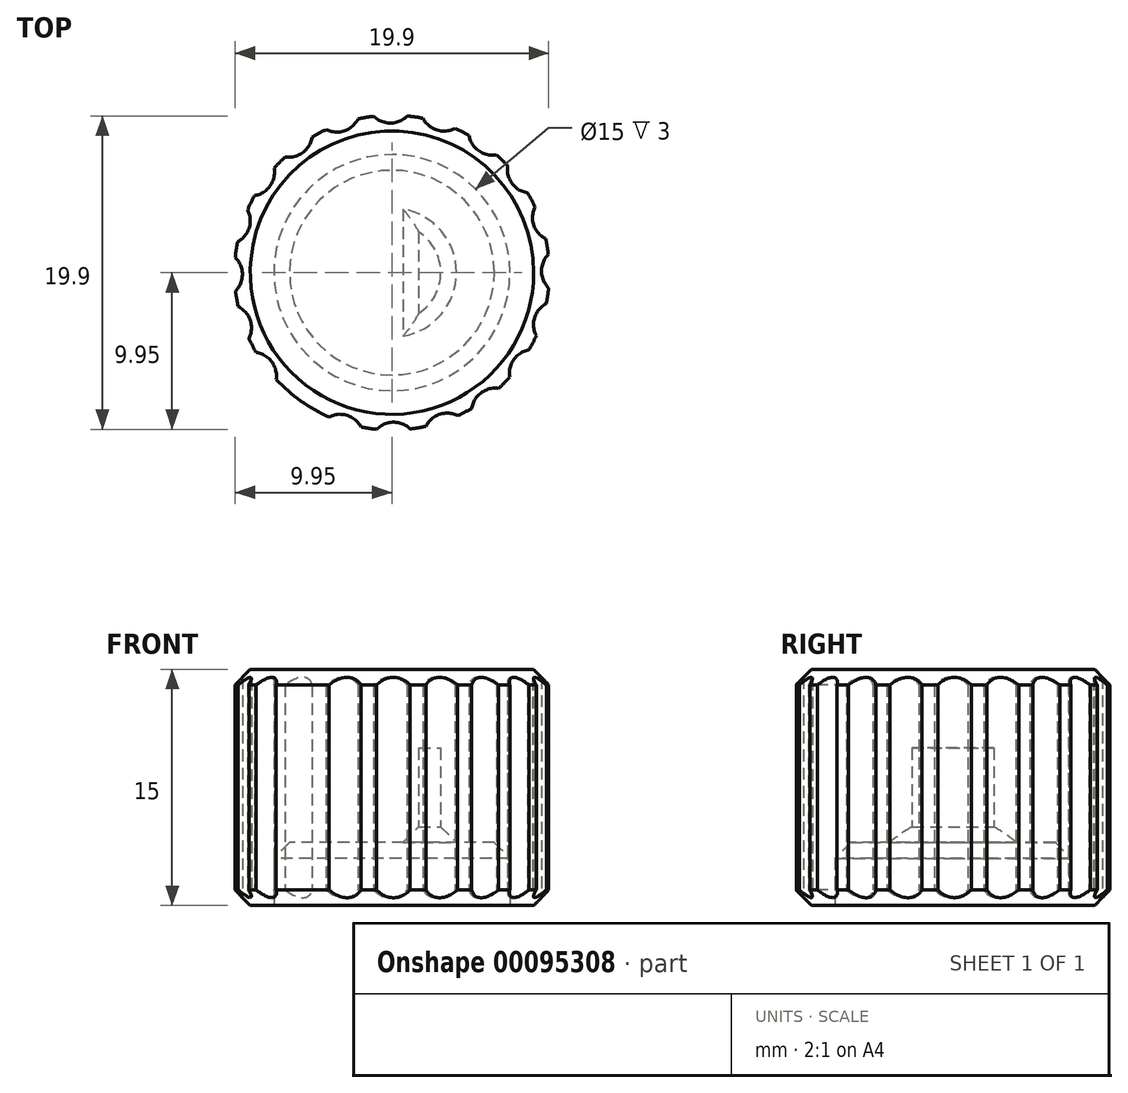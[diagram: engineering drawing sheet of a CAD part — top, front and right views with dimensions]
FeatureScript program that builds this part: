
annotation { "Feature Type Name" : "Feature", "Feature Type Description" : "" }
export const myFeature = defineFeature(function(context is Context, id is Id, definition is map)
    precondition{}
    {
        {
            var Q0;
            Q0=qCreatedBy(makeId("Top.planeOp"),FACE);
            var sketch = newSketch(context, id + "F0", { "sketchPlane" : qUnion([Q0])});
            skCircle(sketch, "E0", {"center": v(0, 0) * mm, "radius": 10 * mm});
            skCircle(sketch, "E1", {"center": v(0, 0) * mm, "radius": 3.1 * mm});
            skLineSegment(sketch, "E2", {"start": v(1.7, 3.51) * mm, "end": v(1.7, -4.44) * mm});
            skCircle(sketch, "E3", {"center": v(0, 0) * mm, "radius": 7.5 * mm});
            skCircle(sketch, "E4", {"center": v(0, 0) * mm, "radius": 11 * mm, "construction": true});
            skCircle(sketch, "E5", {"center": v(10.5, -3.3) * mm, "radius": 1.5 * mm});
            skCircle(sketch, "E6.1.0", {"center": v(11, 0.1) * mm, "radius": 1.5 * mm});
            skCircle(sketch, "E6.2.0", {"center": v(10.43, 3.5) * mm, "radius": 1.5 * mm});
            skCircle(sketch, "E6.3.0", {"center": v(8.83, 6.55) * mm, "radius": 1.5 * mm});
            skCircle(sketch, "E6.4.0", {"center": v(6.38, 8.96) * mm, "radius": 1.5 * mm});
            skCircle(sketch, "E6.5.0", {"center": v(3.3, 10.5) * mm, "radius": 1.5 * mm});
            skCircle(sketch, "E6.6.0", {"center": v(-0.1, 11) * mm, "radius": 1.5 * mm});
            skCircle(sketch, "E6.7.0", {"center": v(-3.5, 10.43) * mm, "radius": 1.5 * mm});
            skCircle(sketch, "E6.8.0", {"center": v(-6.55, 8.83) * mm, "radius": 1.5 * mm});
            skCircle(sketch, "E6.9.0", {"center": v(-8.96, 6.38) * mm, "radius": 1.5 * mm});
            skCircle(sketch, "E6.10.0", {"center": v(-10.5, 3.3) * mm, "radius": 1.5 * mm});
            skCircle(sketch, "E6.11.0", {"center": v(-11, -0.1) * mm, "radius": 1.5 * mm});
            skCircle(sketch, "E6.12.0", {"center": v(-10.43, -3.5) * mm, "radius": 1.5 * mm});
            skCircle(sketch, "E6.13.0", {"center": v(-8.83, -6.55) * mm, "radius": 1.5 * mm});
            skCircle(sketch, "E6.14.0", {"center": v(-6.38, -8.96) * mm, "radius": 1.5 * mm});
            skCircle(sketch, "E6.15.0", {"center": v(-3.3, -10.5) * mm, "radius": 1.5 * mm});
            skCircle(sketch, "E6.16.0", {"center": v(0.1, -11) * mm, "radius": 1.5 * mm});
            skCircle(sketch, "E6.17.0", {"center": v(3.5, -10.43) * mm, "radius": 1.5 * mm});
            skLineSegment(sketch, "E6.anchor1", {"start": v(0, 0) * mm, "end": v(10.5, -3.3) * mm, "construction": true});
            skLineSegment(sketch, "E6.anchor2", {"start": v(0, 0) * mm, "end": v(8.96, -6.38) * mm, "construction": true});
            skCircle(sketch, "E7.1.18.0", {"center": v(6.55, -8.83) * mm, "radius": 1.5 * mm});
            skCircle(sketch, "E7.1.19.0", {"center": v(8.96, -6.38) * mm, "radius": 1.5 * mm});
            skSolve(sketch);
        }
        {
            var Q0;
            {var subQ0=sQuery(id+"F0.wireOp",EDGE,"E2");var subQ1=sQuery(id+"F0.wireOp",EDGE,"E1");var subQ2=makeQuery(id+"F0.imprint","INTERSECT",VERTEX,{"disambiguationData":[OD(0.0)],"derivedFrom":[subQ1,subQ0]});Q0=makeQuery(id+"F0.imprint","IMPRINT",FACE,{"disambiguationData":[TD([[makeQuery(id+"F0.imprint","IMPRINT",EDGE,{"disambiguationData":[TD([[subQ2,-1.0]])],"derivedFrom":subQ1}),1.0]])]});}
            var Q1;
            {var subQ0=sQuery(id+"F0.wireOp",EDGE,"E2");var subQ1=sQuery(id+"F0.wireOp",EDGE,"E1");var subQ2=makeQuery(id+"F0.imprint","INTERSECT",VERTEX,{"disambiguationData":[OD(0.0)],"derivedFrom":[subQ1,subQ0]});Q1=makeQuery(id+"F0.imprint","IMPRINT",FACE,{"disambiguationData":[TD([[makeQuery(id+"F0.imprint","IMPRINT",EDGE,{"disambiguationData":[TD([[subQ2,1.0]])],"derivedFrom":subQ1}),1.0]])]});}
            var Q2;
            Q2=makeQuery(id+"F0.imprint","IMPRINT",FACE,{"disambiguationData":[TD([[makeQuery(id+"F0.imprint","IMPRINT",EDGE,{"derivedFrom":sQuery(id+"F0.wireOp",EDGE,"E3")}),1.0]])]});
            var Q3;
            Q3=makeQuery(id+"F0.imprint","IMPRINT",FACE,{"disambiguationData":[TD([[makeQuery(id+"F0.imprint","IMPRINT",EDGE,{"derivedFrom":sQuery(id+"F0.wireOp",EDGE,"E3")}),-1.0]])]});
            var Q4;
            {var subQ0=sQuery(id+"F0.wireOp",EDGE,"E6.14.0");var subQ1=sQuery(id+"F0.wireOp",EDGE,"E0");var subQ2=makeQuery(id+"F0.imprint","INTERSECT",VERTEX,{"disambiguationData":[OD(0.0)],"derivedFrom":[subQ1,subQ0]});Q4=makeQuery(id+"F0.imprint","IMPRINT",FACE,{"disambiguationData":[TD([[makeQuery(id+"F0.imprint","IMPRINT",EDGE,{"disambiguationData":[TD([[subQ2,-1.0]])],"derivedFrom":subQ1}),1.0]])]});}
            var Q5;
            {var subQ0=sQuery(id+"F0.wireOp",EDGE,"E6.15.0");var subQ1=sQuery(id+"F0.wireOp",EDGE,"E0");var subQ2=makeQuery(id+"F0.imprint","INTERSECT",VERTEX,{"disambiguationData":[OD(0.0)],"derivedFrom":[subQ1,subQ0]});Q5=makeQuery(id+"F0.imprint","IMPRINT",FACE,{"disambiguationData":[TD([[makeQuery(id+"F0.imprint","IMPRINT",EDGE,{"disambiguationData":[TD([[subQ2,-1.0]])],"derivedFrom":subQ1}),1.0]])]});}
            var Q6;
            {var subQ0=sQuery(id+"F0.wireOp",EDGE,"E6.16.0");var subQ1=sQuery(id+"F0.wireOp",EDGE,"E0");var subQ2=makeQuery(id+"F0.imprint","INTERSECT",VERTEX,{"disambiguationData":[OD(0.0)],"derivedFrom":[subQ1,subQ0]});Q6=makeQuery(id+"F0.imprint","IMPRINT",FACE,{"disambiguationData":[TD([[makeQuery(id+"F0.imprint","IMPRINT",EDGE,{"disambiguationData":[TD([[subQ2,-1.0]])],"derivedFrom":subQ1}),1.0]])]});}
            var Q7;
            {var subQ0=sQuery(id+"F0.wireOp",EDGE,"E6.1.0");var subQ1=sQuery(id+"F0.wireOp",EDGE,"E0");var subQ2=makeQuery(id+"F0.imprint","INTERSECT",VERTEX,{"disambiguationData":[OD(0.0)],"derivedFrom":[subQ1,subQ0]});Q7=makeQuery(id+"F0.imprint","IMPRINT",FACE,{"disambiguationData":[TD([[makeQuery(id+"F0.imprint","IMPRINT",EDGE,{"disambiguationData":[TD([[subQ2,1.0]])],"derivedFrom":subQ1}),1.0]])]});}
            var Q8;
            {var subQ0=sQuery(id+"F0.wireOp",EDGE,"E6.2.0");var subQ1=sQuery(id+"F0.wireOp",EDGE,"E0");var subQ2=makeQuery(id+"F0.imprint","INTERSECT",VERTEX,{"disambiguationData":[OD(0.0)],"derivedFrom":[subQ1,subQ0]});Q8=makeQuery(id+"F0.imprint","IMPRINT",FACE,{"disambiguationData":[TD([[makeQuery(id+"F0.imprint","IMPRINT",EDGE,{"disambiguationData":[TD([[subQ2,-1.0]])],"derivedFrom":subQ1}),1.0]])]});}
            var Q9;
            {var subQ0=sQuery(id+"F0.wireOp",EDGE,"E6.17.0");var subQ1=sQuery(id+"F0.wireOp",EDGE,"E0");var subQ2=makeQuery(id+"F0.imprint","INTERSECT",VERTEX,{"disambiguationData":[OD(0.0)],"derivedFrom":[subQ1,subQ0]});Q9=makeQuery(id+"F0.imprint","IMPRINT",FACE,{"disambiguationData":[TD([[makeQuery(id+"F0.imprint","IMPRINT",EDGE,{"disambiguationData":[TD([[subQ2,-1.0]])],"derivedFrom":subQ1}),1.0]])]});}
            var Q10;
            {var subQ0=sQuery(id+"F0.wireOp",EDGE,"E7.1.18.0");var subQ1=sQuery(id+"F0.wireOp",EDGE,"E0");var subQ2=makeQuery(id+"F0.imprint","INTERSECT",VERTEX,{"disambiguationData":[OD(0.0)],"derivedFrom":[subQ1,subQ0]});Q10=makeQuery(id+"F0.imprint","IMPRINT",FACE,{"disambiguationData":[TD([[makeQuery(id+"F0.imprint","IMPRINT",EDGE,{"disambiguationData":[TD([[subQ2,-1.0]])],"derivedFrom":subQ1}),1.0]])]});}
            var Q11;
            {var subQ0=sQuery(id+"F0.wireOp",EDGE,"E6.13.0");var subQ1=sQuery(id+"F0.wireOp",EDGE,"E0");var subQ2=makeQuery(id+"F0.imprint","INTERSECT",VERTEX,{"disambiguationData":[OD(0.0)],"derivedFrom":[subQ1,subQ0]});Q11=makeQuery(id+"F0.imprint","IMPRINT",FACE,{"disambiguationData":[TD([[makeQuery(id+"F0.imprint","IMPRINT",EDGE,{"disambiguationData":[TD([[subQ2,-1.0]])],"derivedFrom":subQ1}),1.0]])]});}
            var Q12;
            {var subQ0=sQuery(id+"F0.wireOp",EDGE,"E6.12.0");var subQ1=sQuery(id+"F0.wireOp",EDGE,"E0");var subQ2=makeQuery(id+"F0.imprint","INTERSECT",VERTEX,{"disambiguationData":[OD(0.0)],"derivedFrom":[subQ1,subQ0]});Q12=makeQuery(id+"F0.imprint","IMPRINT",FACE,{"disambiguationData":[TD([[makeQuery(id+"F0.imprint","IMPRINT",EDGE,{"disambiguationData":[TD([[subQ2,-1.0]])],"derivedFrom":subQ1}),1.0]])]});}
            var Q13;
            {var subQ0=sQuery(id+"F0.wireOp",EDGE,"E6.11.0");var subQ1=sQuery(id+"F0.wireOp",EDGE,"E0");var subQ2=makeQuery(id+"F0.imprint","INTERSECT",VERTEX,{"disambiguationData":[OD(0.0)],"derivedFrom":[subQ1,subQ0]});Q13=makeQuery(id+"F0.imprint","IMPRINT",FACE,{"disambiguationData":[TD([[makeQuery(id+"F0.imprint","IMPRINT",EDGE,{"disambiguationData":[TD([[subQ2,-1.0]])],"derivedFrom":subQ1}),1.0]])]});}
            var Q14;
            {var subQ0=sQuery(id+"F0.wireOp",EDGE,"E6.10.0");var subQ1=sQuery(id+"F0.wireOp",EDGE,"E0");var subQ2=makeQuery(id+"F0.imprint","INTERSECT",VERTEX,{"disambiguationData":[OD(0.0)],"derivedFrom":[subQ1,subQ0]});Q14=makeQuery(id+"F0.imprint","IMPRINT",FACE,{"disambiguationData":[TD([[makeQuery(id+"F0.imprint","IMPRINT",EDGE,{"disambiguationData":[TD([[subQ2,-1.0]])],"derivedFrom":subQ1}),1.0]])]});}
            var Q15;
            {var subQ0=sQuery(id+"F0.wireOp",EDGE,"E6.9.0");var subQ1=sQuery(id+"F0.wireOp",EDGE,"E0");var subQ2=makeQuery(id+"F0.imprint","INTERSECT",VERTEX,{"disambiguationData":[OD(0.0)],"derivedFrom":[subQ1,subQ0]});Q15=makeQuery(id+"F0.imprint","IMPRINT",FACE,{"disambiguationData":[TD([[makeQuery(id+"F0.imprint","IMPRINT",EDGE,{"disambiguationData":[TD([[subQ2,-1.0]])],"derivedFrom":subQ1}),1.0]])]});}
            var Q16;
            {var subQ0=sQuery(id+"F0.wireOp",EDGE,"E6.8.0");var subQ1=sQuery(id+"F0.wireOp",EDGE,"E0");var subQ2=makeQuery(id+"F0.imprint","INTERSECT",VERTEX,{"disambiguationData":[OD(0.0)],"derivedFrom":[subQ1,subQ0]});Q16=makeQuery(id+"F0.imprint","IMPRINT",FACE,{"disambiguationData":[TD([[makeQuery(id+"F0.imprint","IMPRINT",EDGE,{"disambiguationData":[TD([[subQ2,-1.0]])],"derivedFrom":subQ1}),1.0]])]});}
            var Q17;
            {var subQ0=sQuery(id+"F0.wireOp",EDGE,"E6.7.0");var subQ1=sQuery(id+"F0.wireOp",EDGE,"E0");var subQ2=makeQuery(id+"F0.imprint","INTERSECT",VERTEX,{"disambiguationData":[OD(0.0)],"derivedFrom":[subQ1,subQ0]});Q17=makeQuery(id+"F0.imprint","IMPRINT",FACE,{"disambiguationData":[TD([[makeQuery(id+"F0.imprint","IMPRINT",EDGE,{"disambiguationData":[TD([[subQ2,-1.0]])],"derivedFrom":subQ1}),1.0]])]});}
            var Q18;
            {var subQ0=sQuery(id+"F0.wireOp",EDGE,"E6.6.0");var subQ1=sQuery(id+"F0.wireOp",EDGE,"E0");var subQ2=makeQuery(id+"F0.imprint","INTERSECT",VERTEX,{"disambiguationData":[OD(0.0)],"derivedFrom":[subQ1,subQ0]});Q18=makeQuery(id+"F0.imprint","IMPRINT",FACE,{"disambiguationData":[TD([[makeQuery(id+"F0.imprint","IMPRINT",EDGE,{"disambiguationData":[TD([[subQ2,-1.0]])],"derivedFrom":subQ1}),1.0]])]});}
            var Q19;
            {var subQ0=sQuery(id+"F0.wireOp",EDGE,"E6.5.0");var subQ1=sQuery(id+"F0.wireOp",EDGE,"E0");var subQ2=makeQuery(id+"F0.imprint","INTERSECT",VERTEX,{"disambiguationData":[OD(0.0)],"derivedFrom":[subQ1,subQ0]});Q19=makeQuery(id+"F0.imprint","IMPRINT",FACE,{"disambiguationData":[TD([[makeQuery(id+"F0.imprint","IMPRINT",EDGE,{"disambiguationData":[TD([[subQ2,-1.0]])],"derivedFrom":subQ1}),1.0]])]});}
            var Q20;
            {var subQ0=sQuery(id+"F0.wireOp",EDGE,"E6.4.0");var subQ1=sQuery(id+"F0.wireOp",EDGE,"E0");var subQ2=makeQuery(id+"F0.imprint","INTERSECT",VERTEX,{"disambiguationData":[OD(0.0)],"derivedFrom":[subQ1,subQ0]});Q20=makeQuery(id+"F0.imprint","IMPRINT",FACE,{"disambiguationData":[TD([[makeQuery(id+"F0.imprint","IMPRINT",EDGE,{"disambiguationData":[TD([[subQ2,-1.0]])],"derivedFrom":subQ1}),1.0]])]});}
            var Q21;
            {var subQ0=sQuery(id+"F0.wireOp",EDGE,"E7.1.19.0");var subQ1=sQuery(id+"F0.wireOp",EDGE,"E0");var subQ2=makeQuery(id+"F0.imprint","INTERSECT",VERTEX,{"disambiguationData":[OD(0.0)],"derivedFrom":[subQ1,subQ0]});Q21=makeQuery(id+"F0.imprint","IMPRINT",FACE,{"disambiguationData":[TD([[makeQuery(id+"F0.imprint","IMPRINT",EDGE,{"disambiguationData":[TD([[subQ2,-1.0]])],"derivedFrom":subQ1}),1.0]])]});}
            var Q22;
            {var subQ0=sQuery(id+"F0.wireOp",EDGE,"E5");var subQ1=sQuery(id+"F0.wireOp",EDGE,"E0");var subQ2=makeQuery(id+"F0.imprint","INTERSECT",VERTEX,{"disambiguationData":[OD(0.0)],"derivedFrom":[subQ1,subQ0]});Q22=makeQuery(id+"F0.imprint","IMPRINT",FACE,{"disambiguationData":[TD([[makeQuery(id+"F0.imprint","IMPRINT",EDGE,{"disambiguationData":[TD([[subQ2,-1.0]])],"derivedFrom":subQ1}),1.0]])]});}
            var Q23;
            {var subQ0=sQuery(id+"F0.wireOp",EDGE,"E6.3.0");var subQ1=sQuery(id+"F0.wireOp",EDGE,"E0");var subQ2=makeQuery(id+"F0.imprint","INTERSECT",VERTEX,{"disambiguationData":[OD(0.0)],"derivedFrom":[subQ1,subQ0]});Q23=makeQuery(id+"F0.imprint","IMPRINT",FACE,{"disambiguationData":[TD([[makeQuery(id+"F0.imprint","IMPRINT",EDGE,{"disambiguationData":[TD([[subQ2,-1.0]])],"derivedFrom":subQ1}),1.0]])]});}
            extrude(context, id + "F1", {"entities" : qUnion([Q0, Q1, Q2, Q3, Q4, Q5, Q6, Q7, Q8, Q9, Q10, Q11, Q12, Q13, Q14, Q15, Q16, Q17, Q18, Q19, Q20, Q21, Q22, Q23]), "depth" : 15 * mm});
        }
        {
            var Q0;
            {var subQ0=sQuery(id+"F0.wireOp",EDGE,"E2");var subQ1=sQuery(id+"F0.wireOp",EDGE,"E1");var subQ2=makeQuery(id+"F0.imprint","INTERSECT",VERTEX,{"disambiguationData":[OD(0.0)],"derivedFrom":[subQ1,subQ0]});Q0=makeQuery(id+"F0.imprint","IMPRINT",FACE,{"disambiguationData":[TD([[makeQuery(id+"F0.imprint","IMPRINT",EDGE,{"disambiguationData":[TD([[subQ2,1.0]])],"derivedFrom":subQ1}),1.0]])]});}
            extrude(context, id + "F2", {"entities" : qUnion([Q0]), "operationType" : NewBodyOperationType.REMOVE, "depth" : 10 * mm});
        }
        {
            var Q0;
            Q0=makeQuery(id+"F0.imprint","IMPRINT",FACE,{"disambiguationData":[TD([[makeQuery(id+"F0.imprint","IMPRINT",EDGE,{"derivedFrom":sQuery(id+"F0.wireOp",EDGE,"E3")}),1.0]])]});
            var Q1;
            {var subQ0=sQuery(id+"F0.wireOp",EDGE,"E2");var subQ1=sQuery(id+"F0.wireOp",EDGE,"E1");var subQ2=makeQuery(id+"F0.imprint","INTERSECT",VERTEX,{"disambiguationData":[OD(0.0)],"derivedFrom":[subQ1,subQ0]});Q1=makeQuery(id+"F0.imprint","IMPRINT",FACE,{"disambiguationData":[TD([[makeQuery(id+"F0.imprint","IMPRINT",EDGE,{"disambiguationData":[TD([[subQ2,-1.0]])],"derivedFrom":subQ1}),1.0]])]});}
            extrude(context, id + "F3", {"entities" : qUnion([Q0, Q1]), "operationType" : NewBodyOperationType.REMOVE, "depth" : 4 * mm});
        }
        {
            var Q0;
            Q0=makeQuery(id+"F3.boolean.opBoolean","COPY",FACE,{"derivedFrom":makeQuery(id+"F3.opExtrude","CAP_FACE",FACE,{"disambiguationData":[OSD([sQuery(id+"F0.wireOp",EDGE,"E1"),sQuery(id+"F0.wireOp",EDGE,"E2"),sQuery(id+"F0.wireOp",EDGE,"E3")])],"isStart":false})});
            var Q1;
            Q1=makeQuery(id+"F1.opExtrude","CAP_EDGE",EDGE,{"disambiguationData":[OSD([sQuery(id+"F0.wireOp",EDGE,"E0")])],"isStart":false});
            var Q2;
            Q2=makeQuery(id+"F1.opExtrude","CAP_EDGE",EDGE,{"disambiguationData":[OSD([sQuery(id+"F0.wireOp",EDGE,"E0")])],"isStart":true});
            chamfer(context, id + "F4", {"entities" : qUnion([Q0, Q1, Q2]), "width" : 1 * mm, "tangentPropagation" : true});
        }
        {
            var Q0;
            {var subQ0=sQuery(id+"F0.wireOp",EDGE,"E6.16.0");var subQ1=sQuery(id+"F0.wireOp",EDGE,"E0");var subQ2=makeQuery(id+"F0.imprint","INTERSECT",VERTEX,{"disambiguationData":[OD(0.0)],"derivedFrom":[subQ1,subQ0]});Q0=makeQuery(id+"F0.imprint","IMPRINT",FACE,{"disambiguationData":[TD([[makeQuery(id+"F0.imprint","IMPRINT",EDGE,{"disambiguationData":[TD([[subQ2,-1.0]])],"derivedFrom":subQ1}),1.0]])]});}
            var Q1;
            {var subQ0=sQuery(id+"F0.wireOp",EDGE,"E6.17.0");var subQ1=sQuery(id+"F0.wireOp",EDGE,"E0");var subQ2=makeQuery(id+"F0.imprint","INTERSECT",VERTEX,{"disambiguationData":[OD(0.0)],"derivedFrom":[subQ1,subQ0]});Q1=makeQuery(id+"F0.imprint","IMPRINT",FACE,{"disambiguationData":[TD([[makeQuery(id+"F0.imprint","IMPRINT",EDGE,{"disambiguationData":[TD([[subQ2,-1.0]])],"derivedFrom":subQ1}),1.0]])]});}
            var Q2;
            {var subQ0=sQuery(id+"F0.wireOp",EDGE,"E7.1.18.0");var subQ1=sQuery(id+"F0.wireOp",EDGE,"E0");var subQ2=makeQuery(id+"F0.imprint","INTERSECT",VERTEX,{"disambiguationData":[OD(0.0)],"derivedFrom":[subQ1,subQ0]});Q2=makeQuery(id+"F0.imprint","IMPRINT",FACE,{"disambiguationData":[TD([[makeQuery(id+"F0.imprint","IMPRINT",EDGE,{"disambiguationData":[TD([[subQ2,-1.0]])],"derivedFrom":subQ1}),1.0]])]});}
            var Q3;
            {var subQ0=sQuery(id+"F0.wireOp",EDGE,"E7.1.19.0");var subQ1=sQuery(id+"F0.wireOp",EDGE,"E0");var subQ2=makeQuery(id+"F0.imprint","INTERSECT",VERTEX,{"disambiguationData":[OD(0.0)],"derivedFrom":[subQ1,subQ0]});Q3=makeQuery(id+"F0.imprint","IMPRINT",FACE,{"disambiguationData":[TD([[makeQuery(id+"F0.imprint","IMPRINT",EDGE,{"disambiguationData":[TD([[subQ2,-1.0]])],"derivedFrom":subQ1}),1.0]])]});}
            var Q4;
            {var subQ0=sQuery(id+"F0.wireOp",EDGE,"E5");var subQ1=sQuery(id+"F0.wireOp",EDGE,"E0");var subQ2=makeQuery(id+"F0.imprint","INTERSECT",VERTEX,{"disambiguationData":[OD(0.0)],"derivedFrom":[subQ1,subQ0]});Q4=makeQuery(id+"F0.imprint","IMPRINT",FACE,{"disambiguationData":[TD([[makeQuery(id+"F0.imprint","IMPRINT",EDGE,{"disambiguationData":[TD([[subQ2,-1.0]])],"derivedFrom":subQ1}),1.0]])]});}
            var Q5;
            {var subQ0=sQuery(id+"F0.wireOp",EDGE,"E6.1.0");var subQ1=sQuery(id+"F0.wireOp",EDGE,"E0");var subQ2=makeQuery(id+"F0.imprint","INTERSECT",VERTEX,{"disambiguationData":[OD(0.0)],"derivedFrom":[subQ1,subQ0]});Q5=makeQuery(id+"F0.imprint","IMPRINT",FACE,{"disambiguationData":[TD([[makeQuery(id+"F0.imprint","IMPRINT",EDGE,{"disambiguationData":[TD([[subQ2,1.0]])],"derivedFrom":subQ1}),1.0]])]});}
            var Q6;
            {var subQ0=sQuery(id+"F0.wireOp",EDGE,"E6.2.0");var subQ1=sQuery(id+"F0.wireOp",EDGE,"E0");var subQ2=makeQuery(id+"F0.imprint","INTERSECT",VERTEX,{"disambiguationData":[OD(0.0)],"derivedFrom":[subQ1,subQ0]});Q6=makeQuery(id+"F0.imprint","IMPRINT",FACE,{"disambiguationData":[TD([[makeQuery(id+"F0.imprint","IMPRINT",EDGE,{"disambiguationData":[TD([[subQ2,-1.0]])],"derivedFrom":subQ1}),1.0]])]});}
            var Q7;
            {var subQ0=sQuery(id+"F0.wireOp",EDGE,"E6.15.0");var subQ1=sQuery(id+"F0.wireOp",EDGE,"E0");var subQ2=makeQuery(id+"F0.imprint","INTERSECT",VERTEX,{"disambiguationData":[OD(0.0)],"derivedFrom":[subQ1,subQ0]});Q7=makeQuery(id+"F0.imprint","IMPRINT",FACE,{"disambiguationData":[TD([[makeQuery(id+"F0.imprint","IMPRINT",EDGE,{"disambiguationData":[TD([[subQ2,-1.0]])],"derivedFrom":subQ1}),1.0]])]});}
            var Q8;
            {var subQ0=sQuery(id+"F0.wireOp",EDGE,"E6.13.0");var subQ1=sQuery(id+"F0.wireOp",EDGE,"E0");var subQ2=makeQuery(id+"F0.imprint","INTERSECT",VERTEX,{"disambiguationData":[OD(0.0)],"derivedFrom":[subQ1,subQ0]});Q8=makeQuery(id+"F0.imprint","IMPRINT",FACE,{"disambiguationData":[TD([[makeQuery(id+"F0.imprint","IMPRINT",EDGE,{"disambiguationData":[TD([[subQ2,-1.0]])],"derivedFrom":subQ1}),1.0]])]});}
            var Q9;
            {var subQ0=sQuery(id+"F0.wireOp",EDGE,"E6.12.0");var subQ1=sQuery(id+"F0.wireOp",EDGE,"E0");var subQ2=makeQuery(id+"F0.imprint","INTERSECT",VERTEX,{"disambiguationData":[OD(0.0)],"derivedFrom":[subQ1,subQ0]});Q9=makeQuery(id+"F0.imprint","IMPRINT",FACE,{"disambiguationData":[TD([[makeQuery(id+"F0.imprint","IMPRINT",EDGE,{"disambiguationData":[TD([[subQ2,-1.0]])],"derivedFrom":subQ1}),1.0]])]});}
            var Q10;
            {var subQ0=sQuery(id+"F0.wireOp",EDGE,"E6.11.0");var subQ1=sQuery(id+"F0.wireOp",EDGE,"E0");var subQ2=makeQuery(id+"F0.imprint","INTERSECT",VERTEX,{"disambiguationData":[OD(0.0)],"derivedFrom":[subQ1,subQ0]});Q10=makeQuery(id+"F0.imprint","IMPRINT",FACE,{"disambiguationData":[TD([[makeQuery(id+"F0.imprint","IMPRINT",EDGE,{"disambiguationData":[TD([[subQ2,-1.0]])],"derivedFrom":subQ1}),1.0]])]});}
            var Q11;
            {var subQ0=sQuery(id+"F0.wireOp",EDGE,"E6.10.0");var subQ1=sQuery(id+"F0.wireOp",EDGE,"E0");var subQ2=makeQuery(id+"F0.imprint","INTERSECT",VERTEX,{"disambiguationData":[OD(0.0)],"derivedFrom":[subQ1,subQ0]});Q11=makeQuery(id+"F0.imprint","IMPRINT",FACE,{"disambiguationData":[TD([[makeQuery(id+"F0.imprint","IMPRINT",EDGE,{"disambiguationData":[TD([[subQ2,-1.0]])],"derivedFrom":subQ1}),1.0]])]});}
            var Q12;
            {var subQ0=sQuery(id+"F0.wireOp",EDGE,"E6.9.0");var subQ1=sQuery(id+"F0.wireOp",EDGE,"E0");var subQ2=makeQuery(id+"F0.imprint","INTERSECT",VERTEX,{"disambiguationData":[OD(0.0)],"derivedFrom":[subQ1,subQ0]});Q12=makeQuery(id+"F0.imprint","IMPRINT",FACE,{"disambiguationData":[TD([[makeQuery(id+"F0.imprint","IMPRINT",EDGE,{"disambiguationData":[TD([[subQ2,-1.0]])],"derivedFrom":subQ1}),1.0]])]});}
            var Q13;
            {var subQ0=sQuery(id+"F0.wireOp",EDGE,"E6.8.0");var subQ1=sQuery(id+"F0.wireOp",EDGE,"E0");var subQ2=makeQuery(id+"F0.imprint","INTERSECT",VERTEX,{"disambiguationData":[OD(0.0)],"derivedFrom":[subQ1,subQ0]});Q13=makeQuery(id+"F0.imprint","IMPRINT",FACE,{"disambiguationData":[TD([[makeQuery(id+"F0.imprint","IMPRINT",EDGE,{"disambiguationData":[TD([[subQ2,-1.0]])],"derivedFrom":subQ1}),1.0]])]});}
            var Q14;
            {var subQ0=sQuery(id+"F0.wireOp",EDGE,"E6.7.0");var subQ1=sQuery(id+"F0.wireOp",EDGE,"E0");var subQ2=makeQuery(id+"F0.imprint","INTERSECT",VERTEX,{"disambiguationData":[OD(0.0)],"derivedFrom":[subQ1,subQ0]});Q14=makeQuery(id+"F0.imprint","IMPRINT",FACE,{"disambiguationData":[TD([[makeQuery(id+"F0.imprint","IMPRINT",EDGE,{"disambiguationData":[TD([[subQ2,-1.0]])],"derivedFrom":subQ1}),1.0]])]});}
            var Q15;
            {var subQ0=sQuery(id+"F0.wireOp",EDGE,"E6.5.0");var subQ1=sQuery(id+"F0.wireOp",EDGE,"E0");var subQ2=makeQuery(id+"F0.imprint","INTERSECT",VERTEX,{"disambiguationData":[OD(0.0)],"derivedFrom":[subQ1,subQ0]});Q15=makeQuery(id+"F0.imprint","IMPRINT",FACE,{"disambiguationData":[TD([[makeQuery(id+"F0.imprint","IMPRINT",EDGE,{"disambiguationData":[TD([[subQ2,-1.0]])],"derivedFrom":subQ1}),1.0]])]});}
            var Q16;
            {var subQ0=sQuery(id+"F0.wireOp",EDGE,"E6.6.0");var subQ1=sQuery(id+"F0.wireOp",EDGE,"E0");var subQ2=makeQuery(id+"F0.imprint","INTERSECT",VERTEX,{"disambiguationData":[OD(0.0)],"derivedFrom":[subQ1,subQ0]});Q16=makeQuery(id+"F0.imprint","IMPRINT",FACE,{"disambiguationData":[TD([[makeQuery(id+"F0.imprint","IMPRINT",EDGE,{"disambiguationData":[TD([[subQ2,-1.0]])],"derivedFrom":subQ1}),1.0]])]});}
            var Q17;
            {var subQ0=sQuery(id+"F0.wireOp",EDGE,"E6.3.0");var subQ1=sQuery(id+"F0.wireOp",EDGE,"E0");var subQ2=makeQuery(id+"F0.imprint","INTERSECT",VERTEX,{"disambiguationData":[OD(0.0)],"derivedFrom":[subQ1,subQ0]});Q17=makeQuery(id+"F0.imprint","IMPRINT",FACE,{"disambiguationData":[TD([[makeQuery(id+"F0.imprint","IMPRINT",EDGE,{"disambiguationData":[TD([[subQ2,-1.0]])],"derivedFrom":subQ1}),1.0]])]});}
            var Q18;
            {var subQ0=sQuery(id+"F0.wireOp",EDGE,"E6.4.0");var subQ1=sQuery(id+"F0.wireOp",EDGE,"E0");var subQ2=makeQuery(id+"F0.imprint","INTERSECT",VERTEX,{"disambiguationData":[OD(0.0)],"derivedFrom":[subQ1,subQ0]});Q18=makeQuery(id+"F0.imprint","IMPRINT",FACE,{"disambiguationData":[TD([[makeQuery(id+"F0.imprint","IMPRINT",EDGE,{"disambiguationData":[TD([[subQ2,-1.0]])],"derivedFrom":subQ1}),1.0]])]});}
            extrude(context, id + "F5", {"entities" : qUnion([Q0, Q1, Q2, Q3, Q4, Q5, Q6, Q7, Q8, Q9, Q10, Q11, Q12, Q13, Q14, Q15, Q16, Q17, Q18]), "operationType" : NewBodyOperationType.REMOVE, "depth" : 15 * mm});
        }
    });
